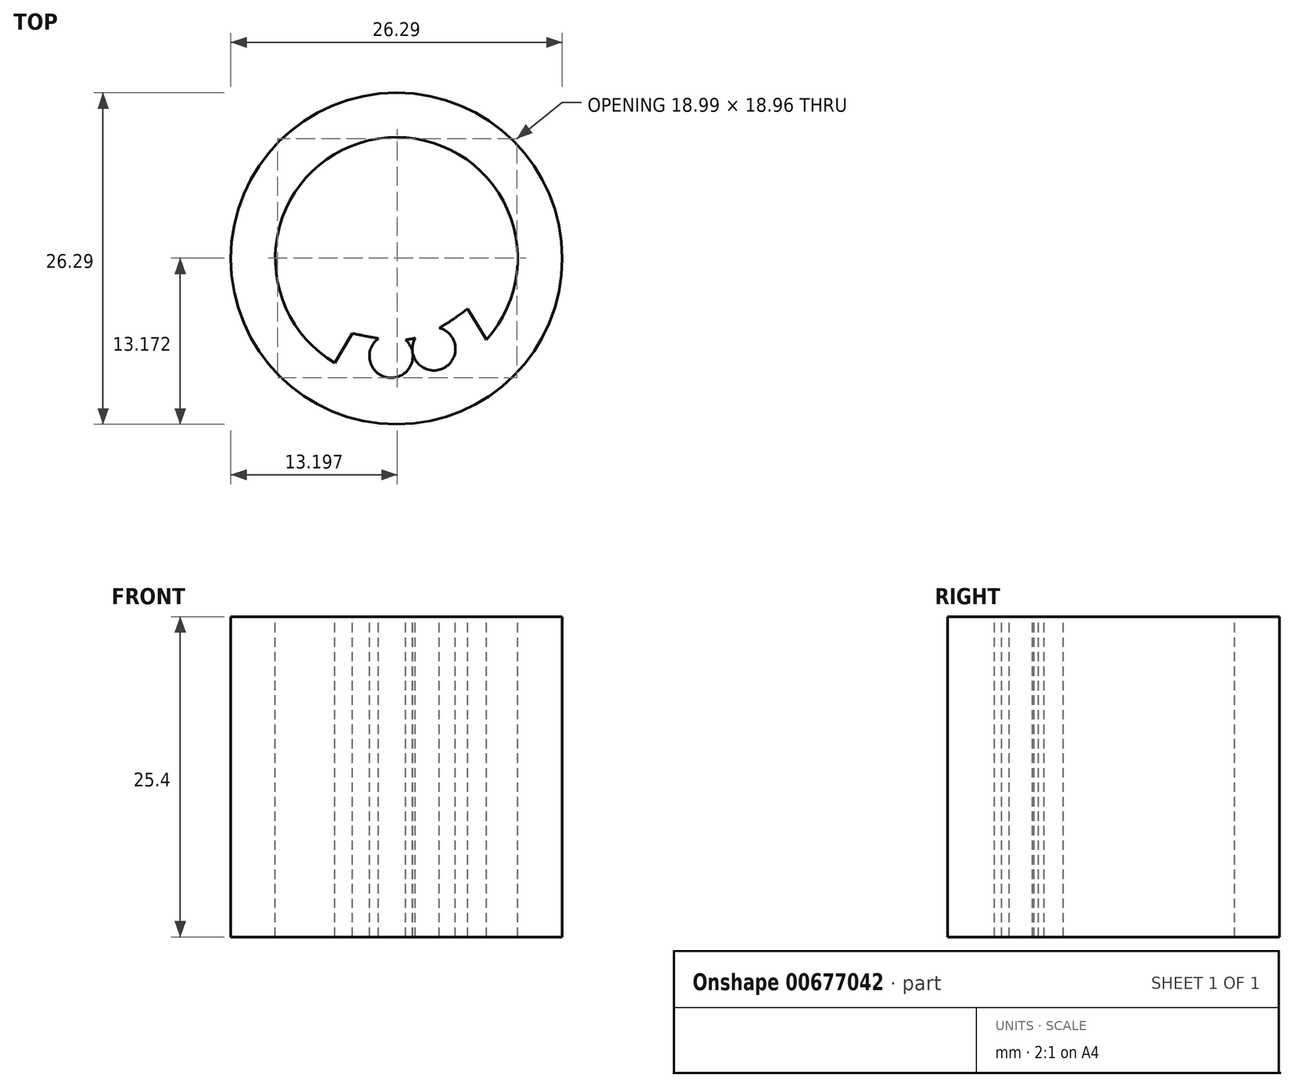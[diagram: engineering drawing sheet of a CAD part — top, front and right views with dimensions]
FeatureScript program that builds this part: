
annotation { "Feature Type Name" : "Feature", "Feature Type Description" : "" }
export const myFeature = defineFeature(function(context is Context, id is Id, definition is map)
    precondition{}
    {
        {
            var Q0;
            Q0=qCreatedBy(makeId("Top.planeOp"),FACE);
            var sketch = newSketch(context, id + "F0", { "sketchPlane" : qUnion([Q0])});
            skCircle(sketch, "E0", {"center": v(22.25, 16.4) * mm, "radius": 13.15 * mm});
            skCircle(sketch, "E1", {"center": v(22.25, 16.4) * mm, "radius": 9.62 * mm});
            skLineSegment(sketch, "E2", {"start": v(17.37, 8.12) * mm, "end": v(18.75, 10.47) * mm});
            skLineSegment(sketch, "E3", {"start": v(23.66, 6.9) * mm, "end": v(23.66, 10.08) * mm});
            skLineSegment(sketch, "E4", {"start": v(29.4, 9.97) * mm, "end": v(27.9, 12.42) * mm});
            skFitSpline(sketch, "E5", {"points": [v(18.75, 10.47) * mm, v(23.66, 10.08) * mm, v(27.9, 12.42) * mm], "startDerivative": vector(9.58, -1.82) * mm, "endDerivative": vector(5.86, 4.28) * mm});
            skSolve(sketch);
        }
        {
            var Q0;
            {var subQ0=sQuery(id+"F0.wireOp",EDGE,"E2");Q0=makeQuery(id+"F0.imprint","IMPRINT",FACE,{"disambiguationData":[TD([[makeQuery(id+"F0.imprint","IMPRINT",EDGE,{"derivedFrom":subQ0}),-1.0]])]});}
            var Q1;
            {var subQ0=sQuery(id+"F0.wireOp",EDGE,"E3");Q1=makeQuery(id+"F0.imprint","IMPRINT",FACE,{"disambiguationData":[TD([[makeQuery(id+"F0.imprint","IMPRINT",EDGE,{"derivedFrom":subQ0}),-1.0]])]});}
            var Q2;
            Q2=makeQuery(id+"F0.imprint","IMPRINT",FACE,{"disambiguationData":[TD([[makeQuery(id+"F0.imprint","IMPRINT",EDGE,{"derivedFrom":sQuery(id+"F0.wireOp",EDGE,"E0")}),1.0]])]});
            extrude(context, id + "F1", {"entities" : qUnion([Q0, Q1, Q2]), "oppositeDirection" : true, "depth" : 25.4 * mm, "offsetDistance" : 25.4 * mm});
        }
        {
            var Q0;
            Q0=makeQuery(id+"F1.opExtrude","CAP_FACE",FACE,{"disambiguationData":[OSD([sQuery(id+"F0.wireOp",EDGE,"E0"),sQuery(id+"F0.wireOp",EDGE,"E1"),sQuery(id+"F0.wireOp",EDGE,"E2"),sQuery(id+"F0.wireOp",EDGE,"E4"),sQuery(id+"F0.wireOp",EDGE,"E5")])],"isStart":true});
            var sketch = newSketch(context, id + "F2", { "sketchPlane" : qUnion([Q0])});
            skCircle(sketch, "E6", {"center": v(21.83, 8.67) * mm, "radius": 1.72 * mm});
            skCircle(sketch, "E7", {"center": v(25.22, 9.24) * mm, "radius": 1.71 * mm});
            skSolve(sketch);
        }
        {
            var Q0;
            Q0=makeQuery(id+"F2.imprint","IMPRINT",FACE,{"disambiguationData":[TD([[makeQuery(id+"F2.imprint","IMPRINT",EDGE,{"derivedFrom":sQuery(id+"F2.wireOp",EDGE,"E6")}),1.0]])]});
            var Q1;
            Q1=makeQuery(id+"F2.imprint","IMPRINT",FACE,{"disambiguationData":[TD([[makeQuery(id+"F2.imprint","IMPRINT",EDGE,{"derivedFrom":sQuery(id+"F2.wireOp",EDGE,"E7")}),1.0]])]});
            extrude(context, id + "F3", {"entities" : qUnion([Q0, Q1]), "operationType" : NewBodyOperationType.REMOVE, "oppositeDirection" : true, "depth" : 25.4 * mm, "offsetDistance" : 25.4 * mm});
        }
    });
